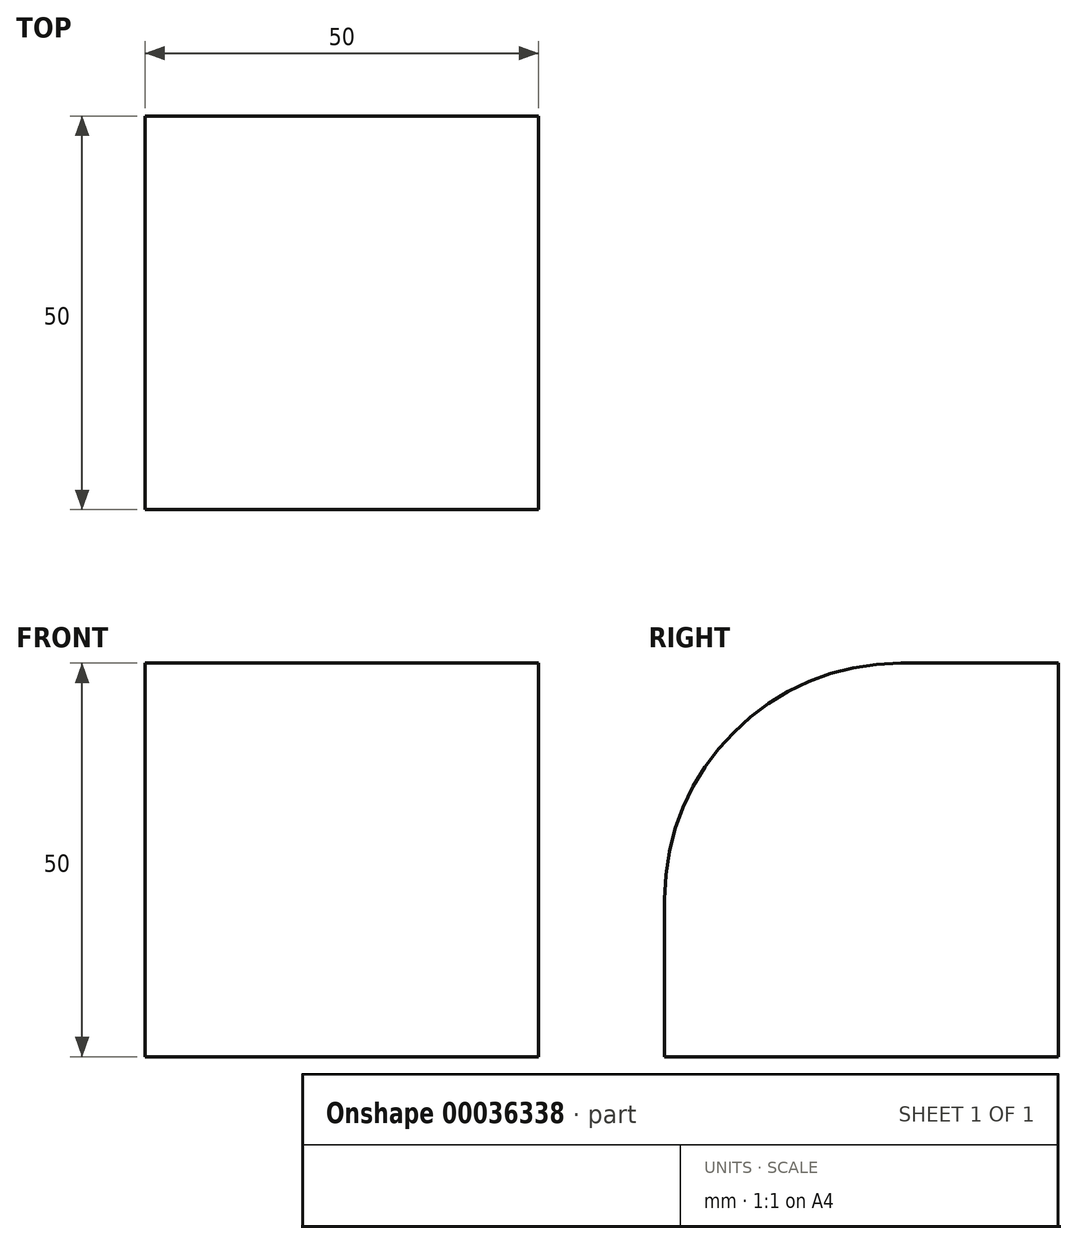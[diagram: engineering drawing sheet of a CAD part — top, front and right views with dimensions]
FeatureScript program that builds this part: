
annotation { "Feature Type Name" : "Feature", "Feature Type Description" : "" }
export const myFeature = defineFeature(function(context is Context, id is Id, definition is map)
    precondition{}
    {
        {
            var Q0;
            Q0=qCreatedBy(makeId("Front.planeOp"),FACE);
            var sketch = newSketch(context, id + "F0", { "sketchPlane" : qUnion([Q0])});
            skLineSegment(sketch, "E0.rect.bottom", {"start": v(25, 25) * mm, "end": v(-25, 25) * mm});
            skLineSegment(sketch, "E0.rect.top", {"start": v(25, -25) * mm, "end": v(-25, -25) * mm});
            skLineSegment(sketch, "E0.rect.left", {"start": v(25, 25) * mm, "end": v(25, -25) * mm});
            skLineSegment(sketch, "E0.rect.right", {"start": v(-25, 25) * mm, "end": v(-25, -25) * mm});
            skPoint(sketch, "E0.rect.middle", {"position": v(0, 0) * mm});
            skSolve(sketch);
        }
        {
            var Q0;
            Q0=makeQuery(id+"F0.imprint","IMPRINT",FACE,{"disambiguationData":[TD([[makeQuery(id+"F0.imprint","IMPRINT",EDGE,{"derivedFrom":sQuery(id+"F0.wireOp",EDGE,"E0.rect.bottom")}),1.0]])]});
            extrude(context, id + "F1", {"entities" : qUnion([Q0]), "depth" : 50 * mm});
        }
        {
            var Q0;
            Q0=makeQuery(id+"F1.opExtrude","CAP_EDGE",EDGE,{"disambiguationData":[OSD([sQuery(id+"F0.wireOp",EDGE,"E0.rect.bottom")])],"isStart":false});
            fillet(context, id + "F2", {"entities" : qUnion([Q0]), "radius" : 30 * mm, "tangentPropagation" : true, "allowEdgeOverflow" : false});
        }
    });
